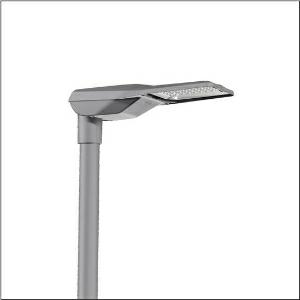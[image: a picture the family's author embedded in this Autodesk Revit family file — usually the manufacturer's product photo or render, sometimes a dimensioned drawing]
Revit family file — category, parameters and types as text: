
# Revit family: streetlight_sl_21_iq_mini___p0_8a_5xe2u31g08jb_9ae4
name_source: partatom
category: Lighting Fixtures
units: mm (PartAtom-declared; Revit-internal decimal feet)

## family parameters
Cut with Voids When Loaded = No
Host = Face
Light Source = No
Part Type = Normal
Room Calculation Point = No
Round Connector Dimension = Use Diameter
Shared = No

## types (1)
- --- (1 x LED, 10920 lm, 71.6 W, 3000K)
    Apparent Load = 72 VA
    CIE Flux Codes = 36 69 97 100 100
    Color Rendering = 70
    Color Temperature = 3000K
    Default Elevation = 1800 mm
    Description = Streetlight SL 21 iQ mini, mast luminaire, primary light control with lens, of PMMA, primary optical cover: cover, of toughened safety glass, transparent, light distribution: P0.8a, light emission: direct distribution, primary light characteristic: asymmetric, installation type: post-top, side-entry, LED, High Power LED, rated luminous flux: 10.920lm, luminous efficacy: 153lm/W, light colour: 730, colour temperature: 3000K, control gear: iQ Street-Remote, control: pre-setting: linear dimming characteristic, Street-Remote, Auto-Match, Temp-Guard, Lumen-Switch, Night-Set, Smart-Wire, Light-Fading, Desk-Remote (wireless, voltage-free reading and setting of iQ features in the workshop via application-optimized NFC function/RFID function), optimised constant luminous flux control (CLO 2.0), mains connection: 220..240V, AC, 50/60Hz, start of lifetime: 72W, end of service life: 75W, reduction: 33W, luminaire housing, of diecast aluminium, powder-coated, Siteco® metallic grey (DB 702S), corrosivity category C5 mid according to DIN EN ISO 12944, please order mast flange separately, inclination adjustable: 0°, 5°, 10°, 15°, sealing non-destructively replaceable, multi-level sealing system, length: 628mm, width: 235mm, height: 110mm, mast flange for spigot size: 42mm (side-entry): 5XC10008XM4, 60/48mm (side-entry/post-top): 5XC10108XM2, 76/60mm (side-entry/post-top): 5XC10108XM1, mounting height: 4..8m, protection rating (complete): IP66, insulation class (complete): insulation class II (safety insulation), certification: CE, ENEC, ENEC+, VDE, impact resistance: IK10, permissible operating ambient temperature for outdoor applications: -40..+50°C, standard-compliant lighting for roads and squares, packaging unit: 1 piece

Light Distribution: P0.8a
    Height = 110 mm
    Lamp = 1 x LED
    Lamp Light Flux = 10920 lm
    Lamp Power = 71.6 W
    Lamp count = 1
    Length = 625 mm
    Luminous efficacy = 153 lm/W
    Manufacturer = Siteco
    ModVariant = No
    Model = 5XE2U31G08JB
    Number of Poles = 1
    OnlyDefault = Yes
    Power Factor = 1
    Product Name = Streetlight SL 21 iQ mini | P0.8a
    Product group = mast luminaire | pylon top
    ProductGroupID = 6100
    Protection Class = Protection class II
    Protection Degree = IP 66
    RLX_Detail_Level = 1
    RLX_Emergency_Light_Flux = 0 lm
    RLX_Emergency_Type = 0
    RLX_Emergency_Type_DB = No
    RlxData = <blob elided: 26105 chars, md5=73678f70>
    Socket = socket
    Standby Power = 0 W
    System Light Flux = 10920 lm
    System Power = 72 W
    Type Comments = factory setting: luminous flux: 100 % | dim-lin: 254 | 746 mA
    Type Image = l_1003519.jpg
    URL = http://relux.com
    VarID = @adj_071596
    Voltage = 0 V
    Weight = 0.00 kg
    Width = 234 mm

## geometry (parser evidence)
native form markers: Blend x4, Sweep x11
no freeform markers — native parametric forms only
